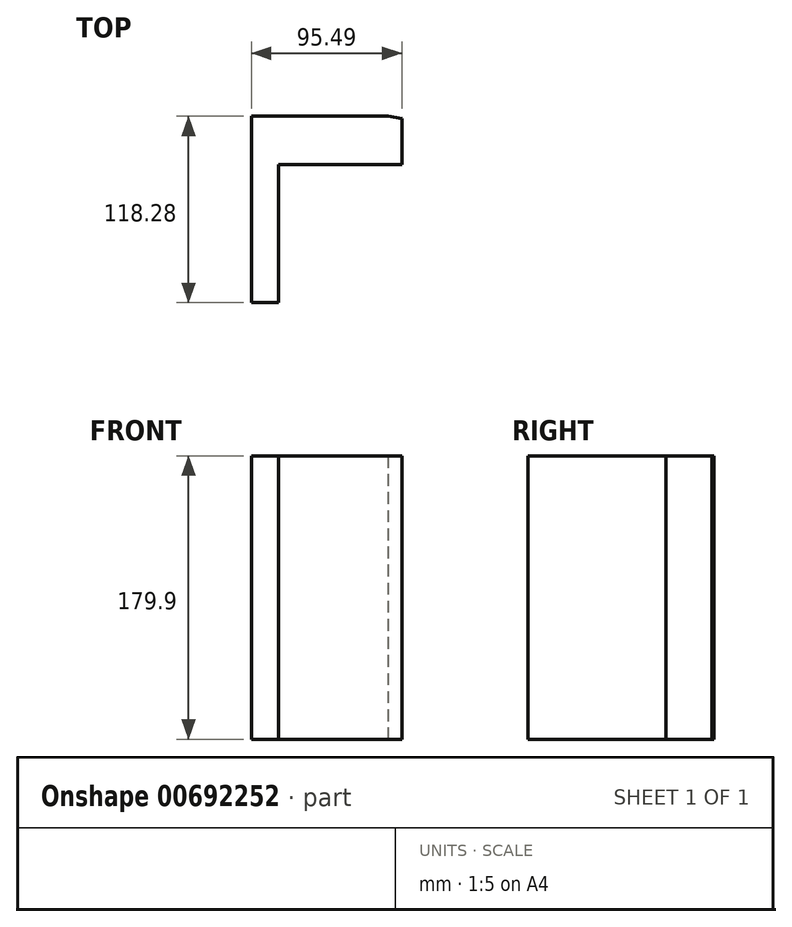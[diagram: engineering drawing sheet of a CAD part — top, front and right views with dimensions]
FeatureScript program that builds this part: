
annotation { "Feature Type Name" : "Feature", "Feature Type Description" : "" }
export const myFeature = defineFeature(function(context is Context, id is Id, definition is map)
    precondition{}
    {
        {
            var Q0;
            Q0=qCreatedBy(makeId("Top.planeOp"),FACE);
            var sketch = newSketch(context, id + "F0", { "sketchPlane" : qUnion([Q0])});
            skLineSegment(sketch, "E0.bottom", {"start": v(0, -50.49) * mm, "end": v(0, -50.49) * mm});
            skLineSegment(sketch, "E0.top", {"start": v(0, -27.42) * mm, "end": v(0, -27.42) * mm});
            skLineSegment(sketch, "E0.left", {"start": v(0, -50.49) * mm, "end": v(0, -27.42) * mm});
            skLineSegment(sketch, "E0.right", {"start": v(0, -50.49) * mm, "end": v(0, -27.42) * mm});
            skLineSegment(sketch, "E1.bottom", {"start": v(19.72, -25.42) * mm, "end": v(21.37, -25.42) * mm});
            skLineSegment(sketch, "E1.top", {"start": v(19.72, -45.2) * mm, "end": v(21.37, -45.2) * mm});
            skLineSegment(sketch, "E1.left", {"start": v(19.72, -25.42) * mm, "end": v(19.72, -45.2) * mm});
            skLineSegment(sketch, "E1.right", {"start": v(21.37, -25.42) * mm, "end": v(21.37, -45.2) * mm});
            skPoint(sketch, "E2.firstSnap0", {"position": v(19.72, -35.3) * mm});
            skLineSegment(sketch, "E2.bottom", {"start": v(5.4, -35.3) * mm, "end": v(29.8, -35.3) * mm});
            skLineSegment(sketch, "E2.top", {"start": v(5.4, -22.82) * mm, "end": v(29.8, -22.82) * mm});
            skLineSegment(sketch, "E2.left", {"start": v(5.4, -35.3) * mm, "end": v(5.4, -22.82) * mm});
            skLineSegment(sketch, "E2.right", {"start": v(29.8, -35.3) * mm, "end": v(29.8, -22.82) * mm});
            skLineSegment(sketch, "E3.bottom", {"start": v(41.01, -53.62) * mm, "end": v(6.62, -53.62) * mm});
            skLineSegment(sketch, "E3.top", {"start": v(41.01, -75.62) * mm, "end": v(6.62, -75.62) * mm});
            skLineSegment(sketch, "E3.left", {"start": v(41.01, -53.62) * mm, "end": v(41.01, -75.62) * mm});
            skLineSegment(sketch, "E3.right", {"start": v(6.62, -53.62) * mm, "end": v(6.62, -75.62) * mm});
            skLineSegment(sketch, "E4.bottom", {"start": v(41.01, -70.44) * mm, "end": v(-54.48, -70.44) * mm});
            skLineSegment(sketch, "E4.top", {"start": v(41.01, 47.84) * mm, "end": v(-54.48, 47.84) * mm});
            skLineSegment(sketch, "E4.left", {"start": v(41.01, -70.44) * mm, "end": v(41.01, 47.84) * mm});
            skLineSegment(sketch, "E4.right", {"start": v(-54.48, -70.44) * mm, "end": v(-54.48, 47.84) * mm});
            skLineSegment(sketch, "E5.bottom", {"start": v(-37.18, 17.26) * mm, "end": v(83, 17.26) * mm});
            skLineSegment(sketch, "E5.top", {"start": v(-37.18, -87.26) * mm, "end": v(83, -87.26) * mm});
            skLineSegment(sketch, "E5.left", {"start": v(-37.18, 17.26) * mm, "end": v(-37.18, -87.26) * mm});
            skLineSegment(sketch, "E5.right", {"start": v(83, 17.26) * mm, "end": v(83, -87.26) * mm});
            skLineSegment(sketch, "E6.bottom", {"start": v(15.9, -129.3) * mm, "end": v(-97.53, -129.3) * mm});
            skLineSegment(sketch, "E6.top", {"start": v(15.9, -85.28) * mm, "end": v(-97.53, -85.28) * mm});
            skLineSegment(sketch, "E6.left", {"start": v(15.9, -129.3) * mm, "end": v(15.9, -85.28) * mm});
            skLineSegment(sketch, "E6.right", {"start": v(-97.53, -129.3) * mm, "end": v(-97.53, -85.28) * mm});
            skLineSegment(sketch, "E7", {"start": v(68.8, 67.13) * mm, "end": v(-18.07, 67.13) * mm});
            skLineSegment(sketch, "E8", {"start": v(-18.07, 67.13) * mm, "end": v(64.36, 55.87) * mm});
            skLineSegment(sketch, "E9", {"start": v(64.36, 55.87) * mm, "end": v(68.8, 67.13) * mm});
            skLineSegment(sketch, "E10", {"start": v(83.35, 89.93) * mm, "end": v(-5, 79.3) * mm});
            skLineSegment(sketch, "E11", {"start": v(-5, 79.3) * mm, "end": v(-16.57, 55.26) * mm});
            skLineSegment(sketch, "E12", {"start": v(-16.57, 55.26) * mm, "end": v(72.77, 41.69) * mm});
            skLineSegment(sketch, "E13", {"start": v(72.77, 41.69) * mm, "end": v(85.77, 90.5) * mm});
            skSolve(sketch);
        }
        {
            var Q0;
            {var subQ0=sQuery(id+"F0.wireOp",EDGE,"E4.right");Q0=makeQuery(id+"F0.imprint","IMPRINT",FACE,{"disambiguationData":[TD([[makeQuery(id+"F0.imprint","IMPRINT",EDGE,{"derivedFrom":subQ0}),-1.0]])]});}
            var sketch = newSketch(context, id + "F1", { "sketchPlane" : qUnion([Q0])});
            skSolve(sketch);
        }
        {
            var Q0;
            {var subQ0=sQuery(id+"F0.wireOp",EDGE,"E4.right");Q0=makeQuery(id+"F1.imprint","IMPRINT",FACE,{"disambiguationData":[TD([[makeQuery(id+"F1.imprint","IMPRINT",EDGE,{"derivedFrom":makeQuery(id+"F0.imprint","IMPRINT",EDGE,{"derivedFrom":subQ0})}),-1.0]])]});}
            extrude(context, id + "F2", {"entities" : qUnion([Q0]), "depth" : 179.9 * mm, "offsetDistance" : 25.4 * mm});
        }
    });
